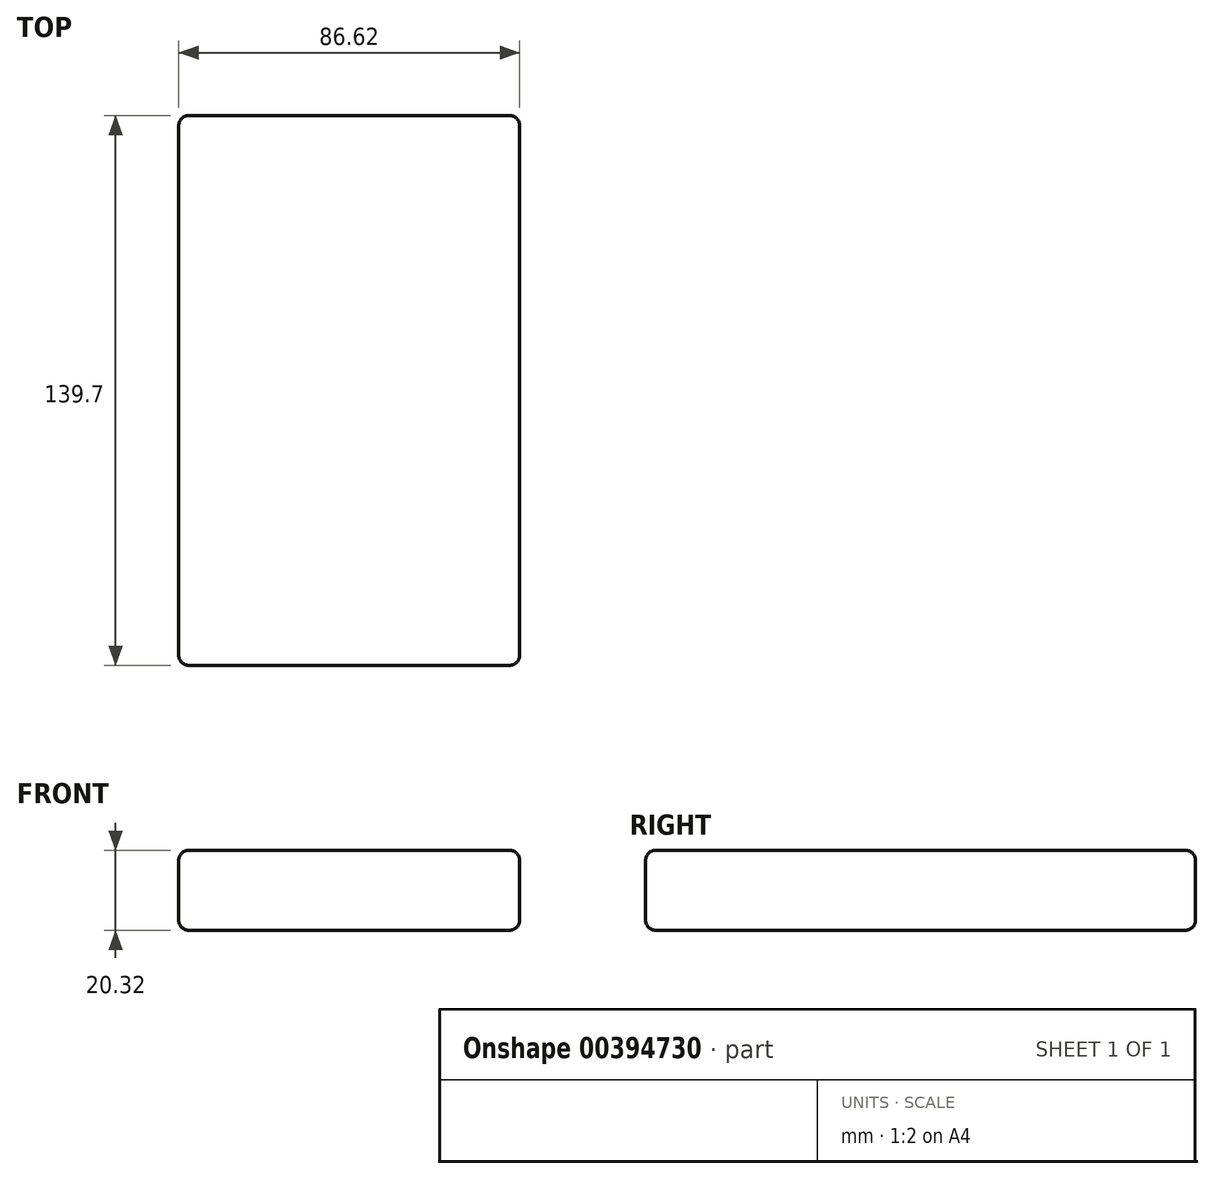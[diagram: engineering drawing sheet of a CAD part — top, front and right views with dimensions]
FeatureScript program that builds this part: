
annotation { "Feature Type Name" : "Feature", "Feature Type Description" : "" }
export const myFeature = defineFeature(function(context is Context, id is Id, definition is map)
    precondition{}
    {
        {
            var Q0;
            Q0=qCreatedBy(makeId("Front.planeOp"),FACE);
            var sketch = newSketch(context, id + "F0", { "sketchPlane" : qUnion([Q0])});
            skLineSegment(sketch, "E0.bottom", {"start": v(57.57, -12.02) * mm, "end": v(-29.05, -12.02) * mm});
            skLineSegment(sketch, "E0.top", {"start": v(57.57, -32.34) * mm, "end": v(-29.05, -32.34) * mm});
            skLineSegment(sketch, "E0.left", {"start": v(57.57, -12.02) * mm, "end": v(57.57, -32.34) * mm});
            skLineSegment(sketch, "E0.right", {"start": v(-29.05, -12.02) * mm, "end": v(-29.05, -32.34) * mm});
            skLineSegment(sketch, "E1.bottom", {"start": v(57.57, -12.02) * mm, "end": v(24.42, -12.02) * mm});
            skLineSegment(sketch, "E1.top", {"start": v(57.57, 54.28) * mm, "end": v(24.42, 54.28) * mm});
            skLineSegment(sketch, "E1.left", {"start": v(57.57, -12.02) * mm, "end": v(57.57, 54.28) * mm});
            skLineSegment(sketch, "E1.right", {"start": v(24.42, -12.02) * mm, "end": v(24.42, 54.28) * mm});
            skLineSegment(sketch, "E2.bottom", {"start": v(-29.05, -12.02) * mm, "end": v(4.1, -12.02) * mm});
            skLineSegment(sketch, "E2.top", {"start": v(-29.05, 54.28) * mm, "end": v(4.1, 54.28) * mm});
            skLineSegment(sketch, "E2.left", {"start": v(-29.05, -12.02) * mm, "end": v(-29.05, 54.28) * mm});
            skLineSegment(sketch, "E2.right", {"start": v(4.1, -12.02) * mm, "end": v(4.1, 54.28) * mm});
            skSolve(sketch);
        }
        {
            var Q0;
            Q0=makeQuery(id+"F0.imprint","IMPRINT",FACE,{"disambiguationData":[TD([[makeQuery(id+"F0.imprint","IMPRINT",EDGE,{"derivedFrom":sQuery(id+"F0.wireOp",EDGE,"E2.bottom")}),1.0]])]});
            var Q1;
            Q1=makeQuery(id+"F0.imprint","IMPRINT",FACE,{"disambiguationData":[TD([[makeQuery(id+"F0.imprint","IMPRINT",EDGE,{"derivedFrom":sQuery(id+"F0.wireOp",EDGE,"E0.bottom")}),1.0]])]});
            var Q2;
            Q2=makeQuery(id+"F0.imprint","IMPRINT",FACE,{"disambiguationData":[TD([[makeQuery(id+"F0.imprint","IMPRINT",EDGE,{"derivedFrom":sQuery(id+"F0.wireOp",EDGE,"E1.bottom")}),-1.0]])]});
            extrude(context, id + "F1", {"entities" : qUnion([Q0, Q1, Q2]), "endBound" : BoundingType.SYMMETRIC, "depth" : 139.7 * mm});
        }
        {
            var Q0;
            Q0=makeQuery(id+"F1.opExtrude","SWEPT_FACE",FACE,{"disambiguationData":[OSD([sQuery(id+"F0.wireOp",EDGE,"E2.top")])]});
            var Q1;
            Q1=makeQuery(id+"F1.opExtrude","SWEPT_FACE",FACE,{"disambiguationData":[OSD([sQuery(id+"F0.wireOp",EDGE,"E1.top")])]});
            var Q2;
            Q2=makeQuery(id+"F1.opExtrude","SWEPT_FACE",FACE,{"disambiguationData":[OSD([sQuery(id+"F0.wireOp",EDGE,"E0.left"),sQuery(id+"F0.wireOp",EDGE,"E1.left")])]});
            var Q3;
            Q3=makeQuery(id+"F1.opExtrude","SWEPT_FACE",FACE,{"disambiguationData":[OSD([sQuery(id+"F0.wireOp",EDGE,"E0.bottom")])]});
            var Q4;
            Q4=makeQuery(id+"F1.opExtrude","SWEPT_FACE",FACE,{"disambiguationData":[OSD([sQuery(id+"F0.wireOp",EDGE,"E2.right")])]});
            var Q5;
            Q5=makeQuery(id+"F1.opExtrude","SWEPT_FACE",FACE,{"disambiguationData":[OSD([sQuery(id+"F0.wireOp",EDGE,"E0.top")])]});
            var Q6;
            Q6=makeQuery(id+"F1.opExtrude","SWEPT_FACE",FACE,{"disambiguationData":[OSD([sQuery(id+"F0.wireOp",EDGE,"E0.right"),sQuery(id+"F0.wireOp",EDGE,"E2.left")])]});
            fillet(context, id + "F2", {"entities" : qUnion([Q0, Q1, Q2, Q3, Q4, Q5, Q6]), "radius" : 2.54 * mm, "tangentPropagation" : true, "allowEdgeOverflow" : false});
        }
    });
